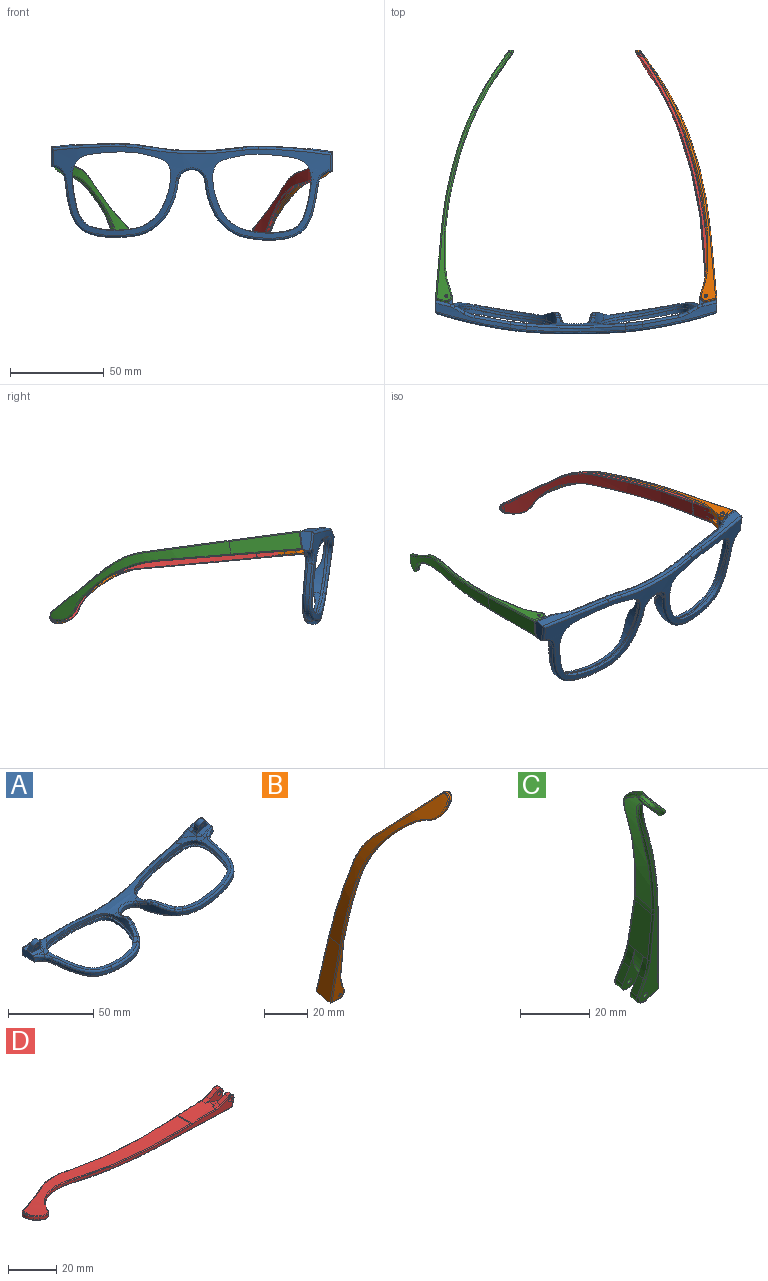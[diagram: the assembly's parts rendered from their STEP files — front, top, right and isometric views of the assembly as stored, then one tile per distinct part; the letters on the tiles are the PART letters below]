
ASSEMBLY  parts=4 mates=3
PART A: 140 faces, bbox 180.4x57.7x41.1 mm
  f0: extruded ~41.43x15.71mm, area 99.8mm2, adj f1,f2,f4,f6,f34,f36,f41
  f1: extruded ~31.5x2.09mm, area 58mm2, adj f0,f3,f4,f41
  f2: extruded ~33.51x12.38mm, area 70.9mm2, adj f0,f3,f6,f8,f10,f41
  f3: extruded ~29.15x10.08mm, area 100.4mm2, adj f1,f2,f4,f7,f8,f9,f11,f12
  f4: cylinder r=255.5mm len=113.95mm, axis (0,1,0), area 521.6mm2, adj f0,f1,f3,f15,f34,f66,f67,f68
  f5: plane 8.8x8.46mm, normal (0.13,-0.25,0.96), area 44.6mm2, adj f22,f28,f32,f33,f35,f37,f38,f73
  f6: cylinder r=255.5mm len=49.95mm, axis (0,1,0), area 171.1mm2, adj f0,f2,f10,f35,f36,f54,f55,f56
  f7: plane 2x1.91mm, normal (0.02,0.48,0.88), area 3mm2, adj f3,f12,f15,f62
  f8: plane 8.58x5.98mm, normal (-0.19,-0.25,0.95), area 17.7mm2, adj f2,f3,f10,f11,f58
  f9: plane 1.75x1.37mm, normal (-0.13,0,0.99), area 1.6mm2, adj f3,f11,f12,f60
  f10: bspline ~5.47x5.23mm, area 9.9mm2, adj f2,f6,f8,f57
  f11: cylinder r=15mm len=4.26mm, axis (0.96,-0.26,0.13), area 6.3mm2, adj f3,f8,f9,f59
  f12: cylinder r=7.5mm len=4.09mm, axis (0.96,-0.26,0.13), area 6.3mm2, adj f3,f7,f9,f61
  f13: plane 7.02x5.65mm, normal (0.39,-0.22,0.89), area 20.8mm2, adj f32,f33,f34,f37,f38,f39,f71
  f14: cylinder r=260mm len=146.62mm, axis (0,1,0), area 1394.7mm2, adj f24,f25,f26,f27,f43,f44,f45,f46
  f15: bspline ~8.04x5.62mm, area 19.7mm2, adj f3,f4,f7,f63,f64,f65
  f16: cylinder r=7.27mm len=7.82mm, axis (0.13,0,-0.99), area 21mm2, adj f19,f22,f52,f53,f54
  f17: extruded ~9.17x4.19mm, area 17.9mm2, adj f18,f23,f44,f68
  f18: cylinder r=160.55mm len=52.75mm, axis (0.13,0,-0.99), area 106.2mm2, adj f17,f43,f67,f89
  f19: extruded ~29.6x20.88mm, area 82.6mm2, adj f16,f21,f51,f55,f56
  f20: cylinder r=7.17mm len=13.61mm, axis (0.13,0,-0.99), area 34.8mm2, adj f47,f48,f65,f66,f116,f133
  f21: extruded ~40.81x31.65mm, area 175.3mm2, adj f19,f47,f50,f51,f56,f57,f58,f59
  f22: plane 10.13x6.13mm, normal (-0.99,0,-0.13), area 50.2mm2, adj f5,f16,f23,f35,f45,f46,f52,f53
  f23: cylinder r=240mm len=40.97mm, axis (0.13,0,-0.99), area 99mm2, adj f17,f22,f46,f69,f70,f71,f72,f73
  f24: extruded ~40.44x15.28mm, area 71.4mm2, adj f14,f25,f26,f40
  f25: extruded ~31.29x1.93mm, area 23.6mm2, adj f14,f24,f27,f40
  f26: extruded ~33x12.12mm, area 47.3mm2, adj f14,f24,f27,f40
  f27: extruded ~28.43x9.7mm, area 57.5mm2, adj f14,f25,f26,f40
  f28: plane 4.75x4.22mm, normal (-0.95,-0.11,0.29), area 14.1mm2, adj f5,f30,f32,f33
  f29: plane 4.55x4.25mm, normal (0.97,-0.03,0.23), area 13.2mm2, adj f30,f32,f33,f39
  f30: cylinder r=3.15mm len=6.18mm, axis (-0.03,0.97,0.26), area 27.5mm2, adj f28,f29,f32,f33
  f31: cylinder r=0.9mm len=3.7mm, axis (-0.03,0.97,0.26), area 18.9mm2, adj f32,f33
  f32: plane 9.71x7.56mm, normal (0.03,-0.97,-0.26), area 40.7mm2, adj f5,f13,f28,f29,f30,f31,f37,f39
  f33: plane 9.71x7.56mm, normal (-0.03,0.97,0.26), area 40.7mm2, adj f5,f13,f28,f29,f30,f31,f38,f39
  f34: bspline ~12.35x10.64mm, area 38.7mm2, adj f0,f4,f13,f36,f70
  f35: bspline ~8.55x2.88mm, area 8.9mm2, adj f5,f6,f22,f36,f53
  f36: bspline ~6.61x6.54mm, area 14.3mm2, adj f0,f6,f34,f35,f37
  f37: cylinder r=10mm len=3.31mm, axis (-0.03,0.97,0.26), area 6.1mm2, adj f5,f13,f32,f36
  f38: cylinder r=10mm len=2.85mm, axis (-0.03,0.97,0.26), area 6.9mm2, adj f5,f13,f33,f72
  f39: cylinder r=2.2mm len=3.67mm, axis (0.03,-0.97,-0.26), area 7mm2, adj f13,f29,f32,f33
  f40: offset ~66.3x57.73mm, area 159mm2, adj f24,f25,f26,f27,f42
  f41: offset ~64.3x55.73mm, area 879mm2, adj f0,f1,f2,f3,f42
  f42: bspline ~55.06x44.49mm, area 238.9mm2, adj f40,f41
  f43: bspline ~65.38x9.16mm, area 105.2mm2, adj f14,f18,f44,f113
  f44: bspline ~12.93x2.14mm, area 17.5mm2, adj f14,f17,f43,f46
  f45: cylinder r=1.25mm len=9.91mm, axis (0,1,0), area 14.2mm2, adj f14,f22,f46,f52
  f46: bspline ~77.04x8.12mm, area 78.1mm2, adj f14,f22,f23,f44,f45
  f47: cylinder r=5mm len=2.69mm, axis (0.13,0,-0.99), area 3.4mm2, adj f20,f21,f49,f64
  f48: bspline ~16.56x7.48mm, area 36.6mm2, adj f14,f20,f49,f117
  f49: bspline ~4.34x2.1mm, area 3mm2, adj f14,f47,f48,f50
  f50: bspline ~42.99x33.62mm, area 116.4mm2, adj f14,f21,f49,f51
  f51: bspline ~31.05x23.81mm, area 69.2mm2, adj f14,f19,f21,f50,f52
  f52: bspline ~10.23x9.78mm, area 20mm2, adj f14,f16,f22,f45,f51
  f53: bspline ~8.57x4.53mm, area 13.2mm2, adj f16,f22,f35,f54
  f54: bspline ~8.21x4.57mm, area 11.4mm2, adj f6,f16,f53,f55
  f55: bspline ~31.34x22.98mm, area 87.2mm2, adj f6,f19,f54,f56
  f56: bspline ~32.19x9.71mm, area 59.2mm2, adj f6,f19,f21,f55,f57
  f57: bspline ~5.57x5.47mm, area 9mm2, adj f10,f21,f56,f58
  f58: bspline ~12.95x7.76mm, area 18.4mm2, adj f8,f21,f57,f59
  f59: bspline ~7.08x3.48mm, area 7.6mm2, adj f11,f21,f58,f60
  f60: bspline ~5.31x2.77mm, area 2mm2, adj f9,f21,f59,f61
  f61: bspline ~6.96x2.96mm, area 7.3mm2, adj f12,f21,f60,f62
  f62: bspline ~7.03x4.48mm, area 3.5mm2, adj f7,f21,f61,f63
  f63: bspline ~6.49x3.49mm, area 6.9mm2, adj f15,f21,f62,f64
  f64: bspline ~3.4x2.17mm, area 2.9mm2, adj f15,f47,f63,f65
  f65: bspline ~5.69x4.22mm, area 5.2mm2, adj f15,f20,f64,f66
  f66: bspline ~14.61x5mm, area 25.3mm2, adj f4,f20,f65,f133
  f67: bspline ~70.69x10.66mm, area 103.8mm2, adj f4,f18,f68,f134
  f68: bspline ~12.87x2.14mm, area 17.3mm2, adj f4,f17,f67,f69
  f69: bspline ~59.89x4.91mm, area 38.6mm2, adj f4,f23,f68,f70
  f70: bspline ~9.47x3.84mm, area 12.1mm2, adj f23,f34,f69,f71
  f71: bspline ~28.22x12.59mm, area 14.1mm2, adj f13,f23,f70,f72
  f72: bspline ~6.96x3.14mm, area 5.9mm2, adj f23,f38,f71,f73
  f73: bspline ~42.55x7.74mm, area 18.7mm2, adj f5,f22,f23,f72
  f74: extruded ~41.43x16.03mm, area 99.8mm2, adj f4,f75,f76,f79,f104,f106,f111
  f75: extruded ~30.97x10.17mm, area 58mm2, adj f4,f74,f77,f111
  f76: extruded ~33.46x12.76mm, area 70.9mm2, adj f74,f77,f79,f81,f83,f111
  f77: extruded ~29.15x11.26mm, area 100.4mm2, adj f4,f75,f76,f80,f81,f82,f84,f85
  f78: plane 8.8x7.92mm, normal (-0.38,-0.25,0.89), area 44.6mm2, adj f92,f98,f102,f103,f105,f107,f108,f139
  f79: cylinder r=255.5mm len=47.72mm, axis (0,1,0), area 171.1mm2, adj f74,f76,f83,f105,f106,f122,f123,f124
  f80: plane 1.91x1.77mm, normal (-0.24,0.48,0.84), area 3mm2, adj f77,f85,f87,f130
  f81: plane 8.58x6.57mm, normal (-0.06,-0.25,0.97), area 17.7mm2, adj f76,f77,f83,f84,f126
  f82: plane 1.75x1.37mm, normal (-0.13,0,0.99), area 1.6mm2, adj f77,f84,f85,f128
  f83: bspline ~5.47x5.29mm, area 9.9mm2, adj f76,f79,f81,f125
  f84: cylinder r=15mm len=4.26mm, axis (-0.96,-0.26,-0.13), area 6.3mm2, adj f77,f81,f82,f127
  f85: cylinder r=7.5mm len=4.09mm, axis (-0.96,-0.26,-0.13), area 6.3mm2, adj f77,f80,f82,f129
  f86: plane 7.02x5.15mm, normal (-0.6,-0.22,0.76), area 20.8mm2, adj f102,f103,f104,f107,f108,f109,f137
  f87: bspline ~8.04x5.06mm, area 19.7mm2, adj f4,f77,f80,f131,f132,f133
  f88: cylinder r=7.27mm len=7.82mm, axis (0.13,0,-0.99), area 21mm2, adj f90,f92,f120,f121,f122
  f89: extruded ~9.17x4.19mm, area 17.9mm2, adj f18,f93,f113,f134
  f90: extruded ~29.6x20.88mm, area 82.6mm2, adj f88,f91,f119,f123,f124
  f91: extruded ~40.81x31.65mm, area 175.3mm2, adj f90,f116,f118,f119,f124,f125,f126,f127
  f92: plane 10.13x6.13mm, normal (0.99,0,0.13), area 50.2mm2, adj f78,f88,f93,f105,f114,f115,f120,f121
  f93: cylinder r=240mm len=40.97mm, axis (0.13,0,-0.99), area 99mm2, adj f89,f92,f115,f135,f136,f137,f138,f139
  f94: extruded ~40.44x15.46mm, area 71.4mm2, adj f14,f95,f96,f110
  f95: extruded ~30.61x9.54mm, area 23.6mm2, adj f14,f94,f97,f110
  f96: extruded ~32.39x12.12mm, area 47.3mm2, adj f14,f94,f97,f110
  f97: extruded ~28.43x10.03mm, area 57.5mm2, adj f14,f95,f96,f110
  f98: plane 4.28x4.22mm, normal (0.85,-0.11,0.52), area 14.1mm2, adj f78,f100,f102,f103
  f99: plane 4.65x4.25mm, normal (-1,-0.03,-0.03), area 13.2mm2, adj f100,f102,f103,f109
  f100: cylinder r=3.15mm len=5.92mm, axis (-0.03,0.97,0.26), area 27.5mm2, adj f98,f99,f102,f103
  f101: cylinder r=0.9mm len=3.7mm, axis (-0.03,0.97,0.26), area 18.9mm2, adj f102,f103
  f102: plane 8.98x8.81mm, normal (0.03,-0.97,-0.26), area 40.7mm2, adj f78,f86,f98,f99,f100,f101,f107,f109
  f103: plane 8.98x8.81mm, normal (-0.03,0.97,0.26), area 40.7mm2, adj f78,f86,f98,f99,f100,f101,f108,f109
  f104: bspline ~12.35x9.82mm, area 38.7mm2, adj f4,f74,f86,f106,f136
  f105: bspline ~7.99x3.65mm, area 8.9mm2, adj f78,f79,f92,f106,f121
  f106: bspline ~6.61x6.11mm, area 14.3mm2, adj f74,f79,f104,f105,f107
  f107: cylinder r=10mm len=3.31mm, axis (-0.03,0.97,0.26), area 6.1mm2, adj f78,f86,f102,f106
  f108: cylinder r=10mm len=2.85mm, axis (-0.03,0.97,0.26), area 6.9mm2, adj f78,f86,f103,f138
  f109: cylinder r=2.2mm len=3.67mm, axis (0.03,-0.97,-0.26), area 7mm2, adj f86,f99,f102,f103
  f110: offset ~63.89x57.73mm, area 159mm2, adj f94,f95,f96,f97,f112
  f111: offset ~61.89x55.73mm, area 879mm2, adj f74,f75,f76,f77,f112
  f112: bspline ~53.5x44.49mm, area 238.9mm2, adj f110,f111
  f113: bspline ~12.81x4.41mm, area 17.5mm2, adj f14,f43,f89,f115
  f114: cylinder r=1.25mm len=9.91mm, axis (0,1,0), area 14.2mm2, adj f14,f92,f115,f120
  f115: bspline ~73.21x26.35mm, area 78.1mm2, adj f14,f92,f93,f113,f114
  f116: cylinder r=5mm len=2.69mm, axis (0.13,0,-0.99), area 3.4mm2, adj f20,f91,f117,f132
  f117: bspline ~4.34x2.26mm, area 3mm2, adj f14,f48,f116,f118
  f118: bspline ~41.94x33.64mm, area 116.5mm2, adj f14,f91,f117,f119
  f119: bspline ~31.05x22.67mm, area 69.2mm2, adj f14,f90,f91,f118,f120
  f120: bspline ~9.78x9.49mm, area 20mm2, adj f14,f88,f92,f114,f119
  f121: bspline ~8.2x4.65mm, area 13.2mm2, adj f88,f92,f105,f122
  f122: bspline ~8.21x4.63mm, area 11.4mm2, adj f79,f88,f121,f123
  f123: bspline ~30.19x21.38mm, area 87.2mm2, adj f79,f90,f122,f124
  f124: bspline ~31.36x9.71mm, area 59.2mm2, adj f79,f90,f91,f123,f125
  f125: bspline ~5.47x5.46mm, area 9mm2, adj f83,f91,f124,f126
  f126: bspline ~12.95x8.45mm, area 18.4mm2, adj f81,f91,f125,f127
  f127: bspline ~8.41x4.25mm, area 7.6mm2, adj f84,f91,f126,f128
  f128: bspline ~5.31x2.61mm, area 2mm2, adj f82,f91,f127,f129
  f129: bspline ~6.96x3.18mm, area 7.3mm2, adj f85,f91,f128,f130
  f130: bspline ~7.03x4.9mm, area 3.5mm2, adj f80,f91,f129,f131
  f131: bspline ~7.68x4.7mm, area 6.9mm2, adj f87,f91,f130,f132
  f132: bspline ~4.27x2.49mm, area 2.9mm2, adj f87,f116,f131,f133
  f133: bspline ~5.69x3.83mm, area 5.2mm2, adj f20,f66,f87,f132
  f134: bspline ~12.75x4.39mm, area 17.3mm2, adj f4,f67,f89,f135
  f135: bspline ~57.41x19.21mm, area 38.6mm2, adj f4,f93,f134,f136
  f136: bspline ~8.89x5.92mm, area 12.1mm2, adj f93,f104,f135,f137
  f137: bspline ~24.82x19.15mm, area 14.1mm2, adj f86,f93,f136,f138
  f138: bspline ~6.5x4.49mm, area 5.9mm2, adj f93,f108,f137,f139
  f139: bspline ~40.37x16.71mm, area 18.7mm2, adj f78,f92,f93,f138
PART B: 63 faces, bbox 34.5x65.5x145.4 mm
  f0: plane 8.84x5.38mm, normal (-0.13,0.25,-0.96), area 29.1mm2, adj f1,f5,f6,f24,f25,f26,f37,f62
  f1: cylinder r=3.15mm len=5.02mm, axis (-0.03,0.97,0.26), area 17.8mm2, adj f0,f2,f25,f35
  f2: plane 6.51x4.21mm, normal (0.91,-0.08,0.41), area 17.7mm2, adj f1,f4,f25,f33
  f3: cylinder r=0.9mm len=3.61mm, axis (-0.03,0.97,0.26), area 18.4mm2, adj f12,f25
  f4: cylinder r=25mm len=7.66mm, axis (0.03,-0.97,-0.26), area 20mm2, adj f2,f8,f25,f31
  f5: plane 38.9x16.39mm, normal (-1,-0.02,-0.05), area 297.1mm2, adj f0,f10,f39,f61,f62
  f6: cylinder r=3.15mm len=5.03mm, axis (-0.03,0.97,0.26), area 17.5mm2, adj f0,f7,f26,f60
  f7: plane 6.47x3.76mm, normal (0.91,-0.08,0.41), area 15.6mm2, adj f6,f22,f26,f58
  f8: plane 21.16x11.83mm, normal (0.99,0,0.13), area 148.2mm2, adj f4,f22,f23,f27,f29,f54
  f9: cylinder r=197.75mm len=105.67mm, axis (-0.03,0.97,0.26), area 554.7mm2, adj f23,f32,f34,f36,f38,f40,f42,f44
  f10: cylinder r=200mm len=107.47mm, axis (-0.03,0.97,0.26), area 566.2mm2, adj f5,f41,f43,f45,f47,f49,f51,f53
  f11: cylinder r=0.9mm len=3.56mm, axis (-0.03,0.97,0.26), area 17.9mm2, adj f13,f26
  f12: plane 82.91x22.11mm, normal (-0.03,0.97,0.26), area 178.3mm2, adj f3,f21,f29,f30,f31,f32,f33,f35
  f13: plane 76.21x16.16mm, normal (0.03,-0.98,-0.21), area 170mm2, adj f11,f14,f50,f52,f54,f56,f58,f59
  f14: cylinder r=63.92mm len=38.36mm, axis (-1,-0.02,-0.05), area 50.5mm2, adj f13,f15,f48,f57
  f15: cylinder r=25mm len=7.11mm, axis (-1,-0.02,-0.05), area 9.3mm2, adj f14,f16,f46,f55
  f16: plane 1.45x0.97mm, normal (0.05,-0.32,-0.94), area 1.2mm2, adj f15,f17,f44,f53
  f17: cylinder r=10mm len=8.68mm, axis (-1,-0.02,-0.05), area 13.5mm2, adj f16,f18,f42,f51
  f18: plane 2.25x2.1mm, normal (0.03,-0.99,-0.11), area 2.4mm2, adj f17,f19,f40,f49
  f19: cylinder r=3mm len=5.21mm, axis (-1,-0.02,-0.05), area 9.1mm2, adj f18,f20,f38,f47
  f20: plane 29.75x27.7mm, normal (-0.05,0.72,0.69), area 46.7mm2, adj f19,f21,f36,f45
  f21: cylinder r=37.5mm len=16.72mm, axis (-1,-0.02,-0.05), area 20.9mm2, adj f12,f20,f34,f43
  f22: cylinder r=25mm len=7.54mm, axis (0.03,-0.97,-0.26), area 15mm2, adj f7,f8,f26,f56
  f23: cylinder r=25mm len=7.29mm, axis (-0.03,0.97,0.26), area 16.5mm2, adj f8,f9,f30,f52
  f24: plane 5.73x4.59mm, normal (0.92,0.13,-0.37), area 18.9mm2, adj f0,f25,f26,f28
  f25: plane 17.15x8.15mm, normal (0.03,-0.97,-0.26), area 54.8mm2, adj f0,f1,f2,f3,f4,f24,f27,f28
  f26: plane 17.15x8.15mm, normal (-0.03,0.97,0.26), area 54.8mm2, adj f0,f6,f7,f11,f22,f24,f27,f28
  f27: cylinder r=37.65mm len=7.96mm, axis (0.03,-0.97,-0.26), area 25.6mm2, adj f8,f25,f26,f28
  f28: cylinder r=15mm len=5.57mm, axis (0.03,-0.97,-0.26), area 17.4mm2, adj f24,f25,f26,f27
  f29: cylinder r=0.6mm len=19.22mm, axis (-0.13,-0.26,0.96), area 18.8mm2, adj f8,f12,f30,f31
  f30: torus R=25.6mm, axis (0.03,-0.97,-0.26), area 2.3mm2, adj f12,f23,f29,f32
  f31: torus R=25.6mm, axis (0.03,-0.97,-0.26), area 7.2mm2, adj f4,f12,f29,f33
  f32: torus R=198.35mm, axis (0.03,-0.97,-0.26), area 43.9mm2, adj f9,f12,f30,f34
  f33: cylinder r=0.6mm len=5.97mm, axis (-0.42,-0.25,0.87), area 6.3mm2, adj f2,f12,f31,f35
  f34: bspline ~21.76x11.15mm, area 19.4mm2, adj f9,f21,f32,f36
  f35: torus R=2.55mm, axis (0.03,-0.97,-0.26), area 5.9mm2, adj f1,f12,f33,f37
  f36: bspline ~30.28x28.03mm, area 46.3mm2, adj f9,f20,f34,f38
  f37: cylinder r=0.6mm len=5.14mm, axis (0.99,0.07,-0.12), area 4.7mm2, adj f0,f12,f35,f39
  f38: bspline ~5.86x4.53mm, area 8.7mm2, adj f9,f19,f36,f40
  f39: cylinder r=0.6mm len=36.82mm, axis (0.04,0.26,-0.97), area 35.6mm2, adj f5,f12,f37,f41
  f40: bspline ~2.25x1.56mm, area 2.3mm2, adj f9,f18,f38,f42
  f41: torus R=199.4mm, axis (0.03,-0.97,-0.26), area 45.3mm2, adj f10,f12,f39,f43
  f42: bspline ~10.09x7.36mm, area 10.2mm2, adj f9,f17,f40,f44
  f43: bspline ~23.83x13.59mm, area 17.7mm2, adj f10,f21,f41,f45
  f44: bspline ~1.21x0.8mm, area 0.7mm2, adj f9,f16,f42,f46
  f45: bspline ~29.98x28.19mm, area 35.7mm2, adj f10,f20,f43,f47
  f46: bspline ~12.17x7.07mm, area 6.4mm2, adj f9,f15,f44,f48
  f47: bspline ~5.48x3.6mm, area 5mm2, adj f10,f19,f45,f49
  f48: bspline ~49.68x31.18mm, area 42mm2, adj f9,f14,f46,f50
  f49: bspline ~31.45x16.59mm, area 2.1mm2, adj f10,f18,f47,f51
  f50: bspline ~37.72x8.45mm, area 36.5mm2, adj f9,f13,f48,f52
  f51: bspline ~10.67x8.63mm, area 12.8mm2, adj f10,f17,f49,f53
  f52: bspline ~2.56x1.1mm, area 2.3mm2, adj f13,f23,f50,f54
  f53: bspline ~1.14x1.11mm, area 1.2mm2, adj f10,f16,f51,f55
  f54: cylinder r=0.6mm len=19.59mm, axis (0.13,0.21,-0.97), area 18.8mm2, adj f8,f13,f52,f56
  f55: bspline ~12.24x7.44mm, area 9.6mm2, adj f10,f15,f53,f57
  f56: bspline ~14.51x5.07mm, area 7.1mm2, adj f13,f22,f54,f58
  f57: bspline ~50.06x31.35mm, area 48.2mm2, adj f10,f14,f55,f59
  f58: cylinder r=0.6mm len=6.29mm, axis (0.42,0.2,-0.89), area 6.2mm2, adj f7,f13,f56,f60
  f59: bspline ~72.32x15.64mm, area 37.5mm2, adj f10,f13,f57,f61
  f60: bspline ~4.68x4mm, area 6mm2, adj f6,f13,f58,f62
  f61: cylinder r=0.6mm len=37.25mm, axis (-0.04,-0.21,0.98), area 35.6mm2, adj f5,f13,f59,f62
  f62: cylinder r=0.6mm len=5.18mm, axis (-0.99,-0.06,0.12), area 4.8mm2, adj f0,f5,f13,f60,f61
PART C: 63 faces, bbox 67.5x65.5x134 mm
  f0: plane 8.84x5.04mm, normal (0.38,0.25,-0.89), area 29.1mm2, adj f1,f5,f6,f24,f25,f26,f37,f62
  f1: cylinder r=3.15mm len=4.43mm, axis (-0.03,0.97,0.26), area 17.8mm2, adj f0,f2,f25,f35
  f2: plane 7.04x4.21mm, normal (-0.98,-0.08,0.16), area 17.7mm2, adj f1,f4,f25,f33
  f3: cylinder r=0.9mm len=3.61mm, axis (-0.03,0.97,0.26), area 18.4mm2, adj f12,f25
  f4: cylinder r=25mm len=7.96mm, axis (0.03,-0.97,-0.26), area 20mm2, adj f2,f8,f25,f31
  f5: plane 38.04x16.39mm, normal (0.98,-0.02,0.21), area 297.1mm2, adj f0,f10,f39,f61,f62
  f6: cylinder r=3.15mm len=4.43mm, axis (-0.03,0.97,0.26), area 17.5mm2, adj f0,f7,f26,f60
  f7: plane 7x3.76mm, normal (-0.98,-0.08,0.16), area 15.6mm2, adj f6,f22,f26,f58
  f8: plane 21.18x11.83mm, normal (-0.99,0,-0.13), area 148.2mm2, adj f4,f22,f23,f27,f29,f54
  f9: cylinder r=197.75mm len=96.08mm, axis (-0.03,0.97,0.26), area 554.6mm2, adj f23,f32,f34,f36,f38,f40,f42,f44
  f10: cylinder r=200mm len=97.84mm, axis (-0.03,0.97,0.26), area 566.2mm2, adj f5,f41,f43,f45,f47,f49,f51,f53
  f11: cylinder r=0.9mm len=3.56mm, axis (-0.03,0.97,0.26), area 17.9mm2, adj f13,f26
  f12: plane 80.77x24.67mm, normal (-0.03,0.97,0.26), area 178.3mm2, adj f3,f21,f29,f30,f31,f32,f33,f35
  f13: plane 74.72x21.38mm, normal (0.02,-0.98,-0.21), area 170mm2, adj f11,f14,f50,f52,f54,f56,f58,f59
  f14: cylinder r=63.92mm len=39.91mm, axis (0.98,-0.02,0.21), area 50.5mm2, adj f13,f15,f48,f57
  f15: cylinder r=25mm len=7.11mm, axis (0.98,-0.02,0.21), area 9.3mm2, adj f14,f16,f46,f55
  f16: plane 1.5x0.97mm, normal (0.19,-0.32,-0.93), area 1.2mm2, adj f15,f17,f44,f53
  f17: cylinder r=10mm len=9.48mm, axis (0.98,-0.02,0.21), area 13.5mm2, adj f16,f18,f42,f51
  f18: plane 2.72x1.96mm, normal (0,-0.99,-0.11), area 2.4mm2, adj f17,f19,f40,f49
  f19: cylinder r=3mm len=5.21mm, axis (0.98,-0.02,0.21), area 9.1mm2, adj f18,f20,f38,f47
  f20: plane 27.7x24.91mm, normal (-0.13,0.72,0.68), area 46.7mm2, adj f19,f21,f36,f45
  f21: cylinder r=37.5mm len=17.37mm, axis (0.98,-0.02,0.21), area 20.9mm2, adj f12,f20,f34,f43
  f22: cylinder r=25mm len=7.84mm, axis (0.03,-0.97,-0.26), area 15mm2, adj f7,f8,f26,f56
  f23: cylinder r=25mm len=7.29mm, axis (-0.03,0.97,0.26), area 16.5mm2, adj f8,f9,f30,f52
  f24: plane 5.02x4.59mm, normal (-0.8,0.13,-0.59), area 18.9mm2, adj f0,f25,f26,f28
  f25: plane 17.19x8.62mm, normal (0.03,-0.97,-0.26), area 54.8mm2, adj f0,f1,f2,f3,f4,f24,f27,f28
  f26: plane 17.19x8.62mm, normal (-0.03,0.97,0.26), area 54.8mm2, adj f0,f6,f7,f11,f22,f24,f27,f28
  f27: cylinder r=37.65mm len=7.78mm, axis (0.03,-0.97,-0.26), area 25.6mm2, adj f8,f25,f26,f28
  f28: cylinder r=15mm len=5.12mm, axis (0.03,-0.97,-0.26), area 17.4mm2, adj f24,f25,f26,f27
  f29: cylinder r=0.6mm len=19.37mm, axis (-0.12,-0.26,0.96), area 18.8mm2, adj f8,f12,f30,f31
  f30: torus R=25.6mm, axis (0.03,-0.97,-0.26), area 2.3mm2, adj f12,f23,f29,f32
  f31: torus R=25.6mm, axis (0.03,-0.97,-0.26), area 7.2mm2, adj f4,f12,f29,f33
  f32: torus R=198.35mm, axis (0.03,-0.97,-0.26), area 43.9mm2, adj f9,f12,f30,f34
  f33: cylinder r=0.6mm len=6.44mm, axis (0.18,-0.25,0.95), area 6.3mm2, adj f2,f12,f31,f35
  f34: bspline ~19.65x11.9mm, area 19.4mm2, adj f9,f21,f32,f36
  f35: torus R=2.55mm, axis (0.03,-0.97,-0.26), area 5.9mm2, adj f1,f12,f33,f37
  f36: bspline ~28.03x25.37mm, area 46.3mm2, adj f9,f20,f34,f38
  f37: cylinder r=0.6mm len=4.99mm, axis (-0.93,0.07,-0.37), area 4.7mm2, adj f0,f12,f35,f39
  f38: bspline ~5.67x3.63mm, area 8.7mm2, adj f9,f19,f36,f40
  f39: cylinder r=0.6mm len=35.85mm, axis (0.21,0.26,-0.94), area 35.6mm2, adj f5,f12,f37,f41
  f40: bspline ~2.04x1.98mm, area 2.3mm2, adj f9,f18,f38,f42
  f41: torus R=199.4mm, axis (0.03,-0.97,-0.26), area 45.3mm2, adj f10,f12,f39,f43
  f42: bspline ~8.44x8.36mm, area 10.2mm2, adj f9,f17,f40,f44
  f43: bspline ~21.39x13.59mm, area 17.7mm2, adj f10,f21,f41,f45
  f44: bspline ~1.21x0.95mm, area 0.7mm2, adj f9,f16,f42,f46
  f45: bspline ~28.19x24.88mm, area 35.7mm2, adj f10,f20,f43,f47
  f46: bspline ~12.17x6.58mm, area 6.4mm2, adj f9,f15,f44,f48
  f47: bspline ~5.71x3.84mm, area 5mm2, adj f10,f19,f45,f49
  f48: bspline ~43.78x31.18mm, area 42mm2, adj f9,f14,f46,f50
  f49: bspline ~26.37x24mm, area 2.1mm2, adj f10,f18,f47,f51
  f50: bspline ~35.84x12.64mm, area 36.5mm2, adj f9,f13,f48,f52
  f51: bspline ~9.09x8.95mm, area 12.8mm2, adj f10,f17,f49,f53
  f52: bspline ~2.41x1.1mm, area 2.3mm2, adj f13,f23,f50,f54
  f53: bspline ~1.18x1.11mm, area 1.2mm2, adj f10,f16,f51,f55
  f54: cylinder r=0.6mm len=19.48mm, axis (0.12,0.21,-0.97), area 18.8mm2, adj f8,f13,f52,f56
  f55: bspline ~12.24x6.6mm, area 9.6mm2, adj f10,f15,f53,f57
  f56: bspline ~7.6x2.13mm, area 7.1mm2, adj f13,f22,f54,f58
  f57: bspline ~44.31x31.35mm, area 48.2mm2, adj f10,f14,f55,f59
  f58: cylinder r=0.6mm len=6.66mm, axis (-0.18,0.2,-0.96), area 6.2mm2, adj f7,f13,f56,f60
  f59: bspline ~68.85x23.29mm, area 37.5mm2, adj f10,f13,f57,f61
  f60: bspline ~4.75x4.29mm, area 6mm2, adj f6,f13,f58,f62
  f61: cylinder r=0.6mm len=36.54mm, axis (-0.21,-0.21,0.95), area 35.6mm2, adj f5,f13,f59,f62
  f62: cylinder r=0.6mm len=4.96mm, axis (0.92,-0.06,0.38), area 4.8mm2, adj f0,f5,f13,f60,f61
PART D: 65 faces, bbox 142.7x39.8x38.6 mm
  f0: cylinder r=223mm len=114.12mm, axis (0,1,0), area 783.2mm2, adj f4,f28,f42,f44,f46,f48,f50,f52
  f1: plane 88.44x6.13mm, normal (0.01,1,0), area 165.7mm2, adj f12,f17,f51,f53,f55,f57,f59,f61
  f2: plane 90.81x6.51mm, normal (-0.03,-1,0), area 168.8mm2, adj f6,f21,f29,f30,f31,f32,f34,f36
  f3: cylinder r=225mm len=95.64mm, axis (0,1,0), area 639mm2, adj f5,f26,f31,f33,f35,f37,f39,f41
  f4: plane 4.58x1.31mm, normal (0.43,0,0.91), area 4.7mm2, adj f0,f54,f56
  f5: plane 3.71x0.76mm, normal (-0.43,0,-0.91), area 2.1mm2, adj f3,f43
  f6: cylinder r=38.26mm len=33.79mm, axis (0,0,-1), area 54.6mm2, adj f2,f7,f33,f44
  f7: plane 1.5x0.42mm, normal (0.85,-0.53,0), area 0.7mm2, adj f6,f8,f35,f46
  f8: cylinder r=10mm len=9.59mm, axis (0,0,-1), area 15.8mm2, adj f7,f9,f37,f48
  f9: plane 2.98x2.78mm, normal (-0.11,-0.99,0), area 4.3mm2, adj f8,f10,f39,f50
  f10: cylinder r=3mm len=5.54mm, axis (0,0,-1), area 11.8mm2, adj f9,f11,f41,f43,f45,f52,f54
  f11: plane 29.73x18.33mm, normal (-0.52,0.85,0), area 48.7mm2, adj f10,f12,f47,f56,f58
  f12: cylinder r=38.26mm len=20.42mm, axis (0,0,-1), area 28.8mm2, adj f1,f11,f49,f60
  f13: plane 10.35x6.15mm, normal (0,1,0), area 28.9mm2, adj f14,f16,f21,f22,f23,f24,f25,f27
  f14: plane 3.95x2.09mm, normal (0.27,0,0.96), area 8.6mm2, adj f13,f15,f16,f25
  f15: plane 10.35x6.15mm, normal (0,-1,0), area 28.9mm2, adj f14,f16,f17,f18,f19,f20,f25,f27
  f16: cylinder r=28.12mm len=5.85mm, axis (0,-1,0), area 25mm2, adj f13,f14,f15,f27
  f17: cylinder r=1mm len=2.63mm, axis (0,1,0), area 16.5mm2, adj f1,f15
  f18: cylinder r=2.2mm len=3.21mm, axis (0,1,0), area 11.6mm2, adj f15,f19,f25,f57
  f19: plane 4.29x2.32mm, normal (-0.46,0,0.89), area 11.1mm2, adj f15,f18,f20,f59
  f20: cylinder r=6.5mm len=2.84mm, axis (0,1,0), area 6.9mm2, adj f15,f19,f27,f61
  f21: cylinder r=1mm len=2.59mm, axis (0,1,0), area 16.3mm2, adj f2,f13
  f22: cylinder r=6.5mm len=2.84mm, axis (0,1,0), area 6mm2, adj f13,f23,f27,f36
  f23: plane 4.29x2.24mm, normal (-0.46,0,0.89), area 10.5mm2, adj f13,f22,f24,f34
  f24: cylinder r=2.2mm len=3.21mm, axis (0,1,0), area 11.7mm2, adj f13,f23,f25,f32
  f25: cylinder r=262.63mm len=8.55mm, axis (0,1,0), area 21.7mm2, adj f13,f14,f15,f18,f24,f26,f30,f53
  f26: plane 42.48x8.89mm, normal (0,0,-1), area 338.4mm2, adj f3,f25,f29,f30,f53
  f27: cylinder r=250mm len=15.02mm, axis (0,1,0), area 116.3mm2, adj f13,f15,f16,f20,f22,f28,f38,f40
  f28: cylinder r=15mm len=7.93mm, axis (0,-1,0), area 3.1mm2, adj f0,f27,f40,f64
  f29: cylinder r=0.35mm len=42.49mm, axis (-1,0.03,0), area 23.3mm2, adj f2,f26,f30,f31
  f30: bspline ~27.49x8.66mm, area 2.3mm2, adj f2,f25,f26,f29,f32
  f31: bspline ~67.9x9.27mm, area 26.2mm2, adj f2,f3,f29,f33
  f32: bspline ~3.21x2.79mm, area 2.7mm2, adj f2,f24,f30,f34
  f33: bspline ~40.44x21.97mm, area 24.9mm2, adj f3,f6,f31,f35
  f34: cylinder r=0.35mm len=4.44mm, axis (0.89,-0.03,0.46), area 2.6mm2, adj f2,f23,f32,f36
  f35: bspline ~37x23.37mm, area 0.3mm2, adj f3,f7,f33,f37
  f36: bspline ~3x1.08mm, area 1.7mm2, adj f2,f22,f34,f38
  f37: bspline ~11.84x6.72mm, area 7.1mm2, adj f3,f8,f35,f39
  f38: bspline ~43.51x3.2mm, area 7.5mm2, adj f2,f27,f36,f40
  f39: bspline ~3.09x1.67mm, area 1.8mm2, adj f3,f9,f37,f41
  f40: bspline ~3.27x0.56mm, area 0.2mm2, adj f2,f27,f28,f38,f42
  f41: bspline ~2.97x1.59mm, area 1mm2, adj f3,f10,f39,f43
  f42: bspline ~66.65x5.41mm, area 36.9mm2, adj f0,f2,f40,f44
  f43: bspline ~4.2x0.96mm, area 1.9mm2, adj f5,f10,f41,f45
  f44: bspline ~40.3x21.89mm, area 20.7mm2, adj f0,f6,f42,f46
  f45: bspline ~1.66x1.45mm, area 0.3mm2, adj f3,f10,f43,f47
  f46: bspline ~0.61x0.43mm, area 0.2mm2, adj f0,f7,f44,f48
  f47: bspline ~29.85x18.63mm, area 17.8mm2, adj f3,f11,f45,f49
  f48: bspline ~11.72x6.71mm, area 5.8mm2, adj f0,f8,f46,f50
  f49: bspline ~28.29x8.46mm, area 11.6mm2, adj f3,f12,f47,f51
  f50: bspline ~3.16x1.67mm, area 1.9mm2, adj f0,f9,f48,f52
  f51: bspline ~67.89x9.27mm, area 25mm2, adj f1,f3,f49,f53
  f52: bspline ~2.59x1.46mm, area 0.8mm2, adj f0,f10,f50,f54
  f53: cylinder r=0.35mm len=42.48mm, axis (1,-0.01,0), area 23.3mm2, adj f1,f25,f26,f51,f55
  f54: bspline ~5.15x1.81mm, area 4.2mm2, adj f4,f10,f52,f56
  f55: bspline ~4.09x1.49mm, area 2.2mm2, adj f1,f25,f53,f57
  f56: cylinder r=0.35mm len=0.39mm, axis (-0.79,-0.49,0.37), area 0mm2, adj f4,f11,f54,f58
  f57: bspline ~3.38x3.13mm, area 2.6mm2, adj f1,f18,f55,f59
  f58: bspline ~29.96x18.6mm, area 22.6mm2, adj f0,f11,f56,f60
  f59: cylinder r=0.35mm len=4.46mm, axis (0.89,-0.01,0.46), area 2.7mm2, adj f1,f19,f57,f61
  f60: bspline ~25.13x8.46mm, area 12.6mm2, adj f0,f12,f58,f62
  f61: bspline ~3.01x1.08mm, area 1.7mm2, adj f1,f20,f59,f63
  f62: bspline ~64.39x4.93mm, area 35.5mm2, adj f0,f1,f60,f64
  f63: bspline ~43.5x3.2mm, area 7.5mm2, adj f1,f27,f61,f64
  f64: bspline ~3.26x0.56mm, area 0.2mm2, adj f1,f28,f62,f63
PLACE A rot(axis=(0.04,-0.66,-0.75),174.4deg) t=(24.6,72.42,9.57)mm fixed
PLACE B rot(axis=(0.04,-0.66,-0.75),174.4deg) t=(24.59,72.41,9.5)mm
PLACE C rot(axis=(0.04,-0.66,-0.75),174.4deg) t=(24.59,72.41,9.5)mm
PLACE D rot(axis=(0.6,-0.6,-0.53),110.7deg) t=(64.11,86.02,24.91)mm
MATE fastened A.f100 <-> C.f35  axis (0.02,0.13,0.99) through (-78.99,86.47,29.3)mm
MATE fastened B.f35 <-> A.f30  axis (-0.02,-0.13,-0.99) through (59.46,86.63,26.91)mm
MATE fastened A.f30 <-> D.f17  axis (0.02,0.13,0.99) through (59.46,86.63,26.91)mm
